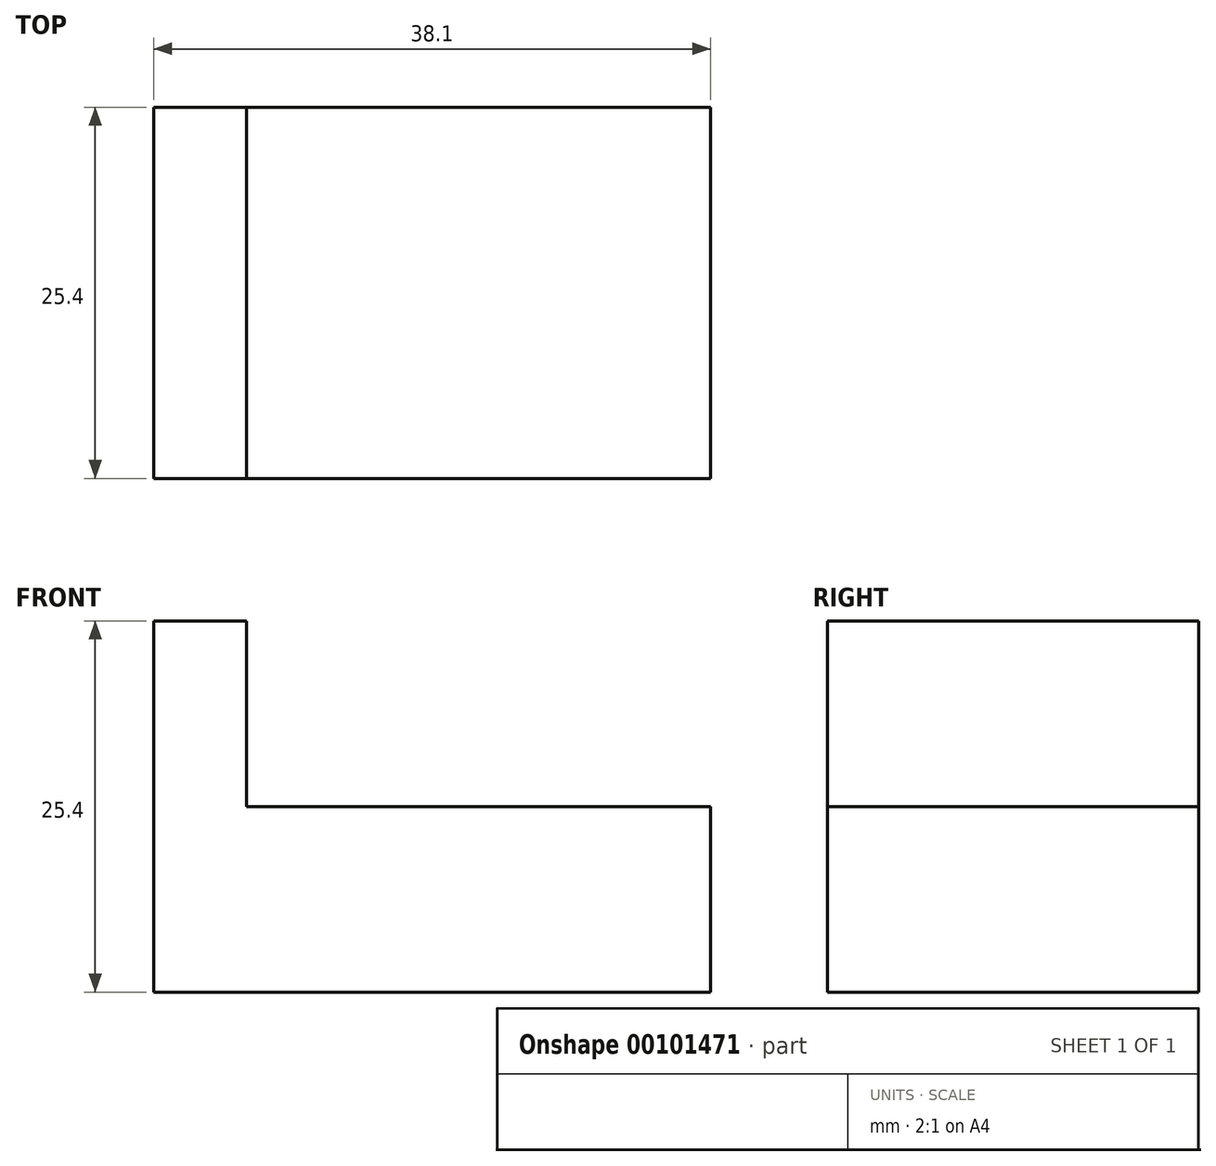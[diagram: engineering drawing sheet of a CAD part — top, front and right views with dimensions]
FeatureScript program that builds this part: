
annotation { "Feature Type Name" : "Feature", "Feature Type Description" : "" }
export const myFeature = defineFeature(function(context is Context, id is Id, definition is map)
    precondition{}
    {
        {
            var Q0;
            Q0=qCreatedBy(makeId("Front.planeOp"),FACE);
            var sketch = newSketch(context, id + "F0", { "sketchPlane" : qUnion([Q0])});
            skLineSegment(sketch, "E0", {"start": v(0, 0) * mm, "end": v(38.1, 0) * mm});
            skLineSegment(sketch, "E1", {"start": v(0, 0) * mm, "end": v(0, 25.4) * mm});
            skLineSegment(sketch, "E2", {"start": v(0, 25.4) * mm, "end": v(6.35, 25.4) * mm});
            skLineSegment(sketch, "E3", {"start": v(6.35, 25.4) * mm, "end": v(6.35, 12.7) * mm});
            skLineSegment(sketch, "E4", {"start": v(6.35, 12.7) * mm, "end": v(38.1, 12.7) * mm});
            skLineSegment(sketch, "E5", {"start": v(38.1, 12.7) * mm, "end": v(38.1, 0) * mm});
            skSolve(sketch);
        }
        {
            var Q0;
            Q0 = qSketchRegion(id + "F0", true);
            extrude(context, id + "F1", {"entities" : qUnion([Q0]), "depth" : 25.4 * mm});
        }
    });
